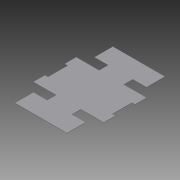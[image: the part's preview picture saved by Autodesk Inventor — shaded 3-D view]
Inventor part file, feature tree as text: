
AUTODESK INVENTOR PART (.ipt)
format: ipt  version: 2015 SP1 (Build 190203100, 203)  size: 129,536 bytes
history: native  units: in
note: dims shown in document units (in); Inventor stores cm internally (conversion verified against a paired STEP export)
features: extrude x2, sketch x2, projected_geometry x1
ambient origin geometry x8: Origin, YZ Plane, XZ Plane, XY Plane, X Axis, Y Axis, Z Axis, Center Point
bodies: Solid1 (feature_tree)
feature tree (5):
  extrude  "Extrusion1"  Depth=32.0in
  extrude  "Extrusion2"  Depth=6.5in
  sketch  "Sketch1"  dims[d0=23.0in d1=32.0in]
  sketch  "Sketch2"  dims[d2=0.125in d3=0.0in d4=6.5in d5=6.5in d6=1.0in d7=1.0in d8=12.75in d9=12.75in d10=3.0in d11=9.0in d12=3.0in d13=9.0in d14=3.0in d15=9.0in d16=3.0in d17=9.0in d18=4.5in d19=3.0in d20=4.5in d21=3.0in d22=4.5in d23=3.0in d24=4.5in d25=3.0in d26=0.125in d27=0.0in]
  projected_geometry  "Projected Loop1"
